# Revit family: Tábua para Cuba Morgana Compact 48 FX
name_source: partatom
category: Modelos genéricos
units: mm (PartAtom-declared; Revit-internal decimal feet)

## family parameters
Com base no plano de trabalho = Não
Compartilhado = Não
Corte com vazios quando carregada = Não
Cota do conector redondo = Utilizar diâmetro
Pode hospedar o vergalhão = Não
Ponto de cálculo do ambiente = Não
Sempre na vertical = Sim
Tipo de parte = Normal

## types (1)
- Tábua para Cuba Morgana Compact 48 FX
    Descrição = Tábua para Cuba de Sobrepor
    Dimensões = 379 x 374 mm
    Elevação padrão = 0 mm  [stored 0 ft]
    Espessura = 18 mm
    Fabricante = Tramontina
    Material predominante = Madeira Teca
    Modelo = Tábua para Cuba Morgana Compact 48 FX
    Referência do produto = 94530/027
    URL do fabricante = tramontina.com.br
    URL do manual de instrução = https://assets.tramontina.com.br
    URL do produto = https://www.tramontina.com.br
    URL dos arquivos BIM = tramontina.com.br/biblioteca
    Usado em conjunto com = Cuba Morgana Compact 48 FX, Cesto Coador em Aço Inox 94532/006

note: [stored X ft] marks values corroborated as IEEE doubles in the binary element streams (Revit-internal decimal feet)
